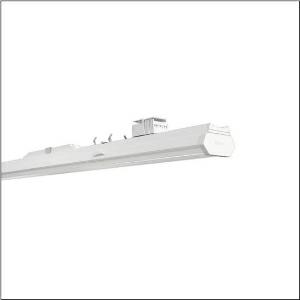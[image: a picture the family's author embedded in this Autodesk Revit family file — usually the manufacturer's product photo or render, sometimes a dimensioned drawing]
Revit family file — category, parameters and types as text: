
# Revit family: licross_r__11_protected_ho_51ts12dn4dxl_19bb
name_source: partatom
category: Lighting Fixtures
units: mm (PartAtom-declared; Revit-internal decimal feet)

## family parameters
Cut with Voids When Loaded = No
Host = Face
Light Source = No
Part Type = Normal
Room Calculation Point = No
Round Connector Dimension = Use Diameter
Shared = No

## types (1)
- --- (1 x LED, 13360 lm, 86.1 W, 4000K)
    Apparent Load = 86 VA
    CIE Flux Codes = 54 82 95 97 100
    Color Rendering = 80
    Color Temperature = 4000K
    Default Elevation = 1800 mm
    Description = Licross® 11 Protected HOluminaire insert, length: 1.500mm, width: 90mm, height: 101mm, LED rated luminous flux: 13.360lm, light colour: 840, control gear: DALI 2, control gear: ECG DALI, with plug, 5-pole, with phase selection, mains connection: 220..240V, AC, 50/60Hz, halogen-free wiring, primary optical cover: cover, of PMMA, light emission: direct with ceiling illumination distribution, protection rating (complete): IP50, insulation class (complete): insulation class I (protective earthing), certification: CE, ENEC, VDE, protection symbol: D if used in an environment with non-conductive dust loads with corresponding accessories, permissible ambient temperature for indoor applications: -25..+35°C, reducing of maximum allowable ambient temperature of 5°C with ceiling mounting, corresponds to IFS (International Featured Standards) requirements for safety and quality in the food industry, packaging unit: 1 piece
    Height = 92 mm
    Lamp = 1 x LED
    Lamp Light Flux = 13360 lm
    Lamp Power = 86.1 W
    Lamp count = 1
    Length = 1500 mm
    Luminous efficacy = 155 lm/W
    Manufacturer = Siteco
    ModVariant = No
    Model = 51TS12DN4DXL
    Mounting Place = Ceiling
    Mounting Type = Pendant
    Number of Poles = 1
    OnlyDefault = Yes
    Power Factor = 1
    Product Name = Licross® 11 Protected HO
    Product group = luminaire insert
    ProductGroupID = 902
    Protection Class = Protection class I
    Protection Degree = IP 50
    RLX_Detail_Level = 1
    RlxData = <blob elided: 24021 chars, md5=4f2151e7>
    Socket = socket
    Standby Power = 0 W
    System Light Flux = 13360 lm
    System Power = 86 W
    Type Comments = factory setting: luminous flux: 100 % | dim-lin: 254 | 485 mA
    Type Image = l_1256145.jpg
    URL = http://relux.com
    VarID = @adj_138285
    Voltage = 0 V
    Weight = 0.00 kg
    Width = 88 mm

## geometry (parser evidence)
native form markers: Blend x4, Sweep x9
no freeform markers — native parametric forms only
